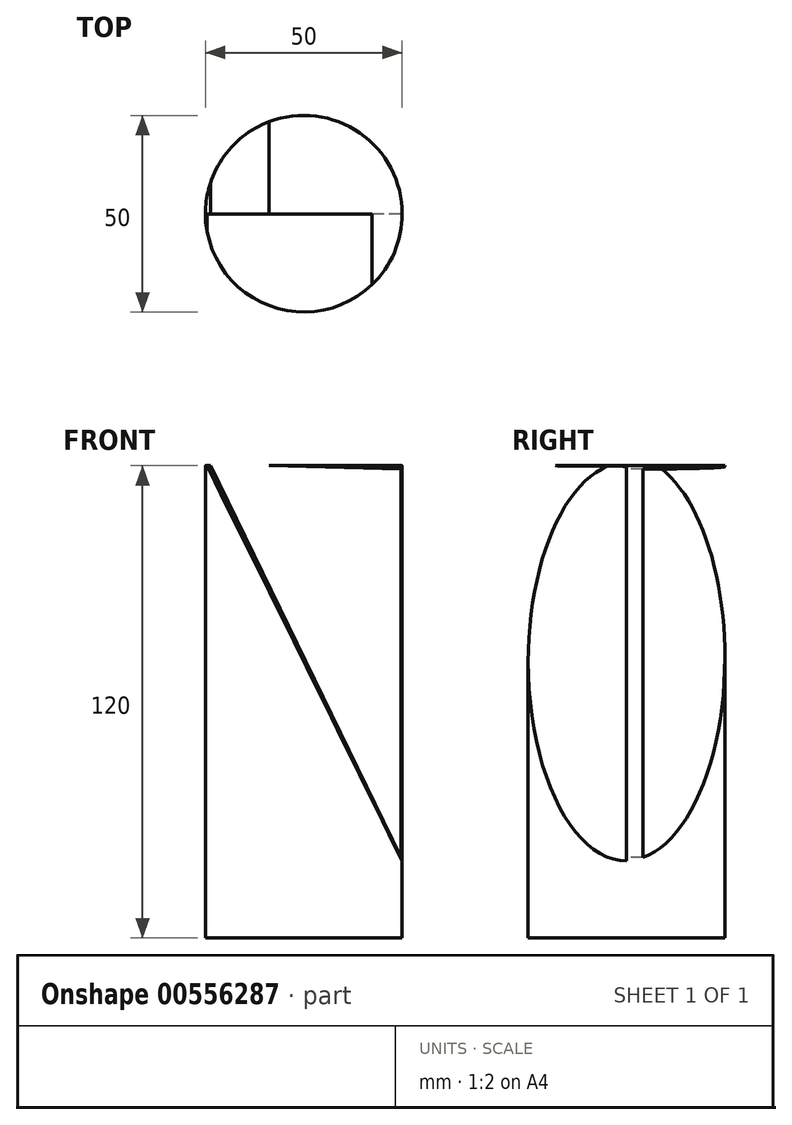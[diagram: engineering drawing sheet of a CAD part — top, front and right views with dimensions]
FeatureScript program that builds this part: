
annotation { "Feature Type Name" : "Feature", "Feature Type Description" : "" }
export const myFeature = defineFeature(function(context is Context, id is Id, definition is map)
    precondition{}
    {
        {
            var Q0;
            Q0=qCreatedBy(makeId("Top.planeOp"),FACE);
            var sketch = newSketch(context, id + "F0", { "sketchPlane" : qUnion([Q0])});
            skCircle(sketch, "E0", {"center": v(0, 0) * mm, "radius": 25 * mm});
            skSolve(sketch);
        }
        {
            var Q0;
            Q0 = qSketchRegion(id + "F0", true);
            extrude(context, id + "F1", {"entities" : qUnion([Q0]), "depth" : 120 * mm, "offsetDistance" : 25 * mm});
        }
        {
            var Q0;
            Q0=qCreatedBy(makeId("Front.planeOp"),FACE);
            var sketch = newSketch(context, id + "F2", { "sketchPlane" : qUnion([Q0])});
            skLineSegment(sketch, "E1", {"start": v(-24.94, 120.71) * mm, "end": v(25.32, 18.94) * mm});
            skLineSegment(sketch, "E2", {"start": v(25.32, 18.94) * mm, "end": v(25.32, 119.87) * mm});
            skLineSegment(sketch, "E3", {"start": v(25.32, 119.87) * mm, "end": v(-24.94, 120.71) * mm});
            skSolve(sketch);
        }
        {
            var Q0;
            Q0 = qSketchRegion(id + "F2", true);
            extrude(context, id + "F3", {"entities" : qUnion([Q0]), "operationType" : NewBodyOperationType.REMOVE, "depth" : 25 * mm, "offsetDistance" : 25 * mm});
        }
        {
            var Q0;
            Q0=qCreatedBy(makeId("Front.planeOp"),FACE);
            var sketch = newSketch(context, id + "F4", { "sketchPlane" : qUnion([Q0])});
            skLineSegment(sketch, "E4", {"start": v(-23.94, 120.39) * mm, "end": v(24.66, 20.5) * mm});
            skLineSegment(sketch, "E5", {"start": v(24.66, 20.5) * mm, "end": v(24.66, 119.15) * mm});
            skLineSegment(sketch, "E6", {"start": v(24.66, 119.15) * mm, "end": v(-23.94, 120.39) * mm});
            skSolve(sketch);
        }
        {
            var Q0;
            Q0 = qSketchRegion(id + "F4", true);
            extrude(context, id + "F5", {"entities" : qUnion([Q0]), "operationType" : NewBodyOperationType.REMOVE, "oppositeDirection" : true, "depth" : 145 * mm, "offsetDistance" : 25 * mm});
        }
    });
